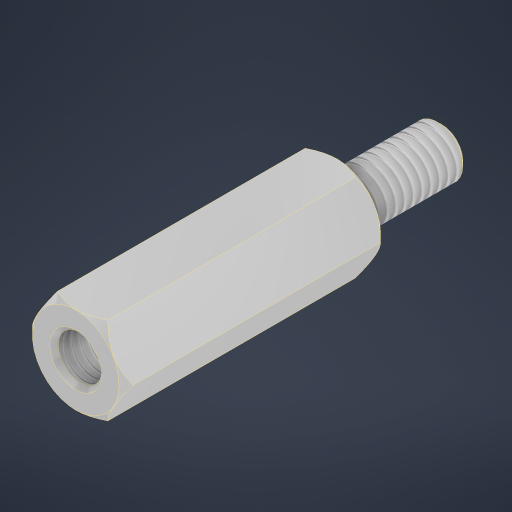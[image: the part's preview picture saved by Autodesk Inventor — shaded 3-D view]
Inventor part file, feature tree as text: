
AUTODESK INVENTOR PART (.ipt)
format: ipt  version: 2023 (Build 270158000, 158)  size: 231,424 bytes
history: native  units: mm
features: thread x2, other x1
ambient origin geometry x8: Origin, YZ Plane, XZ Plane, XY Plane, X Axis, Y Axis, Z Axis, Center Point
bodies: Solid1 (feature_tree)
feature tree (3):
  thread  "Thread1"  [1 undecoded]
  thread  "Thread2"  [1 undecoded]
  other  "InnerChamfer"
note: 2 required parameter values undecoded (feature->parameter linkage not recoverable at this tier; creation-order binding heuristic only, values carry confidence <= 0.55)
